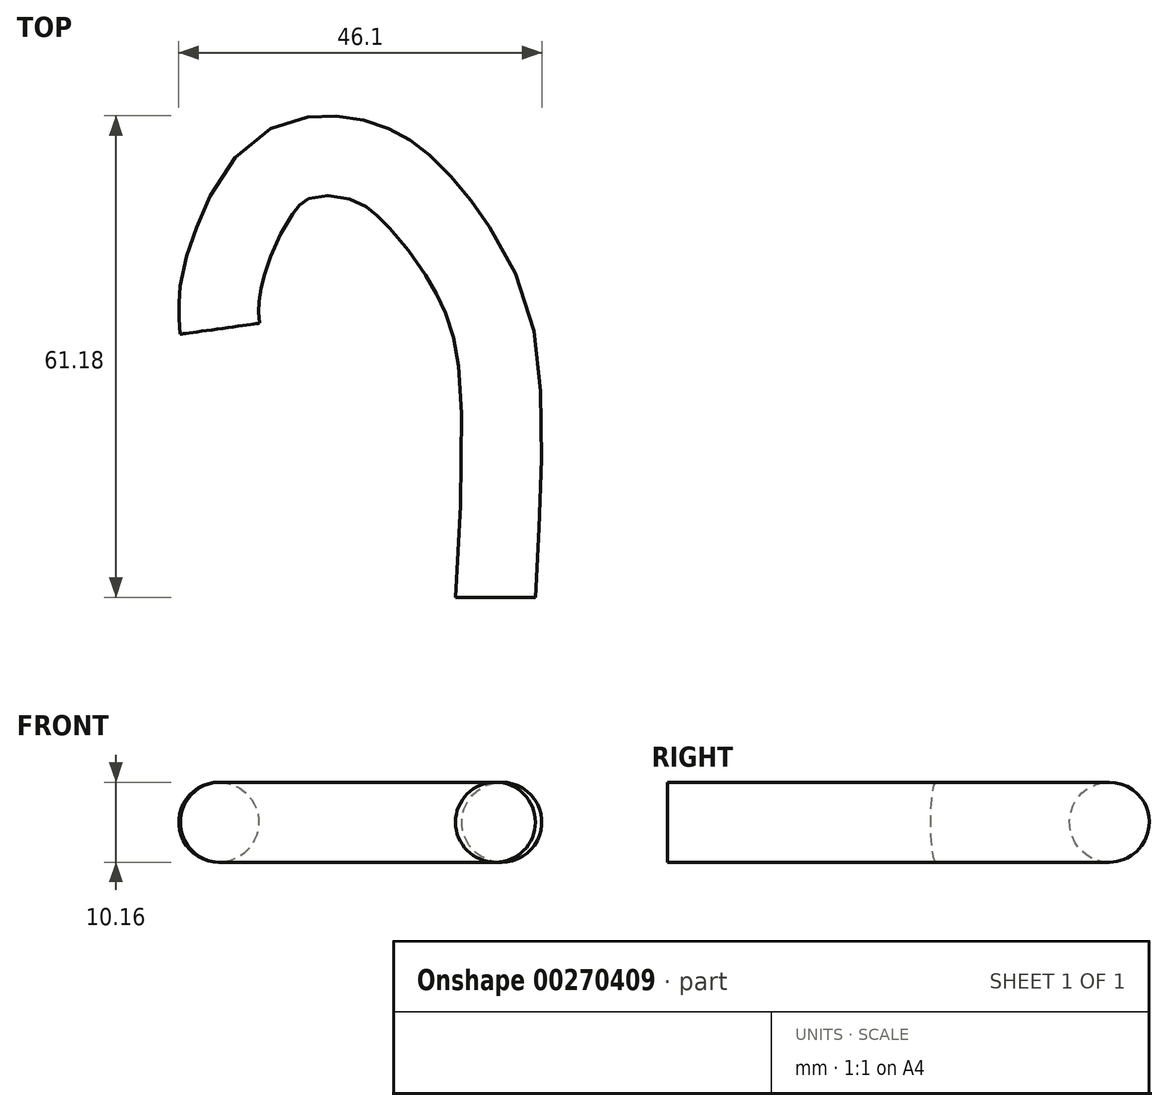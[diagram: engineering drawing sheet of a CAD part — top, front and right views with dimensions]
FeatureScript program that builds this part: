
annotation { "Feature Type Name" : "Feature", "Feature Type Description" : "" }
export const myFeature = defineFeature(function(context is Context, id is Id, definition is map)
    precondition{}
    {
        {
            var Q0;
            Q0=qCreatedBy(makeId("Top.planeOp"),FACE);
            var sketch = newSketch(context, id + "F0", { "sketchPlane" : qUnion([Q0])});
            skPoint(sketch, "E0.middle", {"position": v(0, -40.9) * mm});
            skFitSpline(sketch, "E1", {"points": [v(0, 0) * mm, v(0, 32.3) * mm, v(-4.36, 43.22) * mm, v(-10.12, 50.8) * mm, v(-16.8, 55.36) * mm, v(-26.2, 55.05) * mm, v(-32.27, 47.47) * mm, v(-35, 38.97) * mm, v(-35, 34.12) * mm], "startDerivative": vector(9.75, 170.46) * mm, "endDerivative": vector(4.45, -54.5) * mm});
            skSolve(sketch);
        }
        {
            var Q0;
            Q0=qCreatedBy(makeId("Front.planeOp"),FACE);
            var sketch = newSketch(context, id + "F1", { "sketchPlane" : qUnion([Q0])});
            skCircle(sketch, "E2", {"center": v(0, 0) * mm, "radius": 5.08 * mm});
            skSolve(sketch);
        }
        {
            var Q0;
            Q0=makeQuery(id+"F1.imprint","IMPRINT",FACE,{"disambiguationData":[TD([[makeQuery(id+"F1.imprint","IMPRINT",EDGE,{"derivedFrom":sQuery(id+"F1.wireOp",EDGE,"E2")}),1.0]])]});
            var Q1;
            Q1=sQuery(id+"F0.wireOp",EDGE,"E1");
            sweep(context, id + "F2", {"profiles" : qUnion([Q0]), "path" : qUnion([Q1])});
        }
    });
